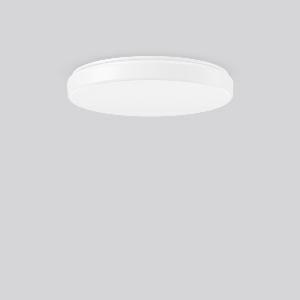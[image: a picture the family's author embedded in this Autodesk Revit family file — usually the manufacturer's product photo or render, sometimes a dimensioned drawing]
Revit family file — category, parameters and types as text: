
# Revit family: flat_polymero_kreis_slim_312240_002_1_76_7999
name_source: partatom
category: Lighting Fixtures
units: mm (PartAtom-declared; Revit-internal decimal feet)

## family parameters
Cut with Voids When Loaded = No
Host = Face
Light Source = No
Part Type = Normal
Room Calculation Point = No
Round Connector Dimension = Use Diameter
Shared = No

## types (1)
- FLAT POLYMERO KREIS SLIM (1 x LED Modul 830, 3050 lm, 3000)
    Apparent Load = 32 VA
    CIE Flux Codes = 41 72 91 83 100
    Color Rendering = 80
    Color Temperature = 3000
    Default Elevation = 1800 mm
    Description = Series: FLAT POLYMERO KREIS SLIM
Flat decorative round LED surface-mounted luminaire. Base: metal, powder-coated. Diffuser made of non-yellowing plastic (PMMA), opal. Diffuser fastening: patented push system. Suitable for Ceiling mounting, Wall (surface). 
Colour: white
Diameter: 460 mm
Height: 70 mm
Lamp: LED exchangeable
Socket: without socket
Colour temperature: 3000K
Colour rendering index (CRI): 83
System power: 32 W
Rated luminous flux: 3050 lm
Luminous efficiency: 95 lm/W
Control gear: AC power, DALI dimmable
Protection class: I
Type of protection: IP 40
    Height = 70 mm
    Lamp = 1 x LED Modul 830
    Lamp Light Flux = 3050 lm
    Lamp count = 1
    Length = 460 mm
    Lifetime = 50000 h
    Luminous efficacy = 95 lm/W
    Manufacturer = RZB
    ModVariant = No
    Model = 312240.002.1.76
    Mounting Place = Ceiling, Wall
    Mounting Type = Surface mounted
    Number of Poles = 1
    OnlyDefault = Yes
    Power Factor = 1
    Product Name = FLAT POLYMERO KREIS SLIM
    Product group = Surface mounted ceiling and wall luminaires
    ProductGroupID = 305
    Protection Class = Protection class I
    Protection Degree = IP 40
    RLX_Detail_Level = 1
    RLX_Emergency_Light_Flux = 0 lm
    RLX_Emergency_Type = 0
    RLX_Emergency_Type_DB = No
    RlxData = <blob elided: 58573 chars, md5=c3e0a8e8>
    Socket = socket
    Standby Power = 0 W
    System Light Flux = 3050 lm
    System Power = 32 W
    Type Comments = Product without accessories
    Type Image = 312086.002.jpg
    URL = http://relux.com
    VarID = ---
    Voltage = 230 V
    Voltage Range = 220-240 V
    Weight = 0.00 kg
    Width = 0 mm  [stored 0 ft]

note: [stored X ft] marks values corroborated as IEEE doubles in the binary element streams (Revit-internal decimal feet)

## geometry (parser evidence)
native form markers: Blend x4, Sweep x13
no freeform markers — native parametric forms only
